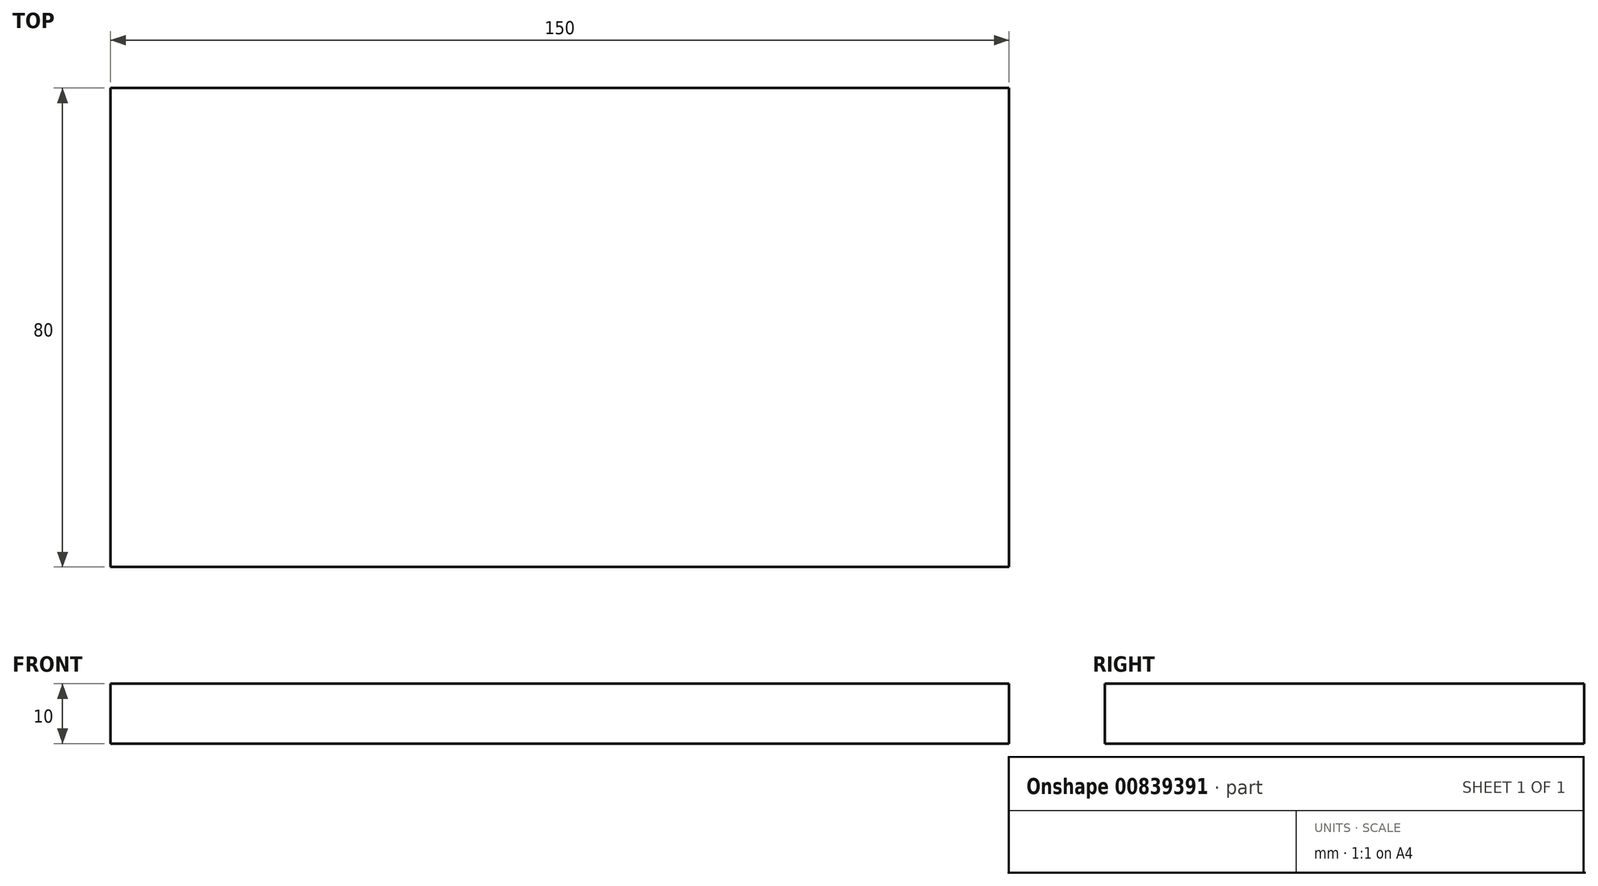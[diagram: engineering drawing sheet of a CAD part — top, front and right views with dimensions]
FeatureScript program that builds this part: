
annotation { "Feature Type Name" : "Feature", "Feature Type Description" : "" }
export const myFeature = defineFeature(function(context is Context, id is Id, definition is map)
    precondition{}
    {
        {
            var Q0;
            Q0=qCreatedBy(makeId("Top.planeOp"),FACE);
            var sketch = newSketch(context, id + "F0", { "sketchPlane" : qUnion([Q0])});
            skLineSegment(sketch, "E0.bottom", {"start": v(-48.92, 49.38) * mm, "end": v(51.08, 49.38) * mm});
            skLineSegment(sketch, "E0.top", {"start": v(-48.92, -50.62) * mm, "end": v(51.08, -50.62) * mm});
            skLineSegment(sketch, "E0.left", {"start": v(-48.92, 49.38) * mm, "end": v(-48.92, -50.62) * mm});
            skLineSegment(sketch, "E0.right", {"start": v(51.08, 49.38) * mm, "end": v(51.08, -50.62) * mm});
            skSolve(sketch);
        }
        {
            var Q0;
            Q0=makeQuery(id+"F0.imprint","IMPRINT",FACE,{"disambiguationData":[TD([[makeQuery(id+"F0.imprint","IMPRINT",EDGE,{"derivedFrom":sQuery(id+"F0.wireOp",EDGE,"E0.bottom")}),-1.0]])]});
            var sketch = newSketch(context, id + "F1", { "sketchPlane" : qUnion([Q0])});
            skLineSegment(sketch, "E1.bottom", {"start": v(-49.26, 49.15) * mm, "end": v(50.74, 49.15) * mm});
            skLineSegment(sketch, "E1.top", {"start": v(-49.26, -50.85) * mm, "end": v(50.74, -50.85) * mm});
            skLineSegment(sketch, "E1.left", {"start": v(-49.26, 49.15) * mm, "end": v(-49.26, -50.85) * mm});
            skLineSegment(sketch, "E1.right", {"start": v(50.74, 49.15) * mm, "end": v(50.74, -50.85) * mm});
            skSolve(sketch);
        }
        {
            var Q0;
            {var subQ0=sQuery(id+"F1.wireOp",EDGE,"E1.right");var subQ1=sQuery(id+"F1.wireOp",EDGE,"E1.bottom");var subQ2=makeQuery(id+"F1.imprint","INTERSECT",VERTEX,{"derivedFrom":[subQ1,subQ0]});Q0=makeQuery(id+"F1.imprint","IMPRINT",FACE,{"disambiguationData":[TD([[makeQuery(id+"F1.imprint","IMPRINT",EDGE,{"disambiguationData":[TD([[subQ2,1.0]])],"derivedFrom":subQ1}),-1.0]])]});}
            var sketch = newSketch(context, id + "F2", { "sketchPlane" : qUnion([Q0])});
            skLineSegment(sketch, "E2.bottom", {"start": v(-39.95, 37.83) * mm, "end": v(110.05, 37.83) * mm});
            skLineSegment(sketch, "E2.top", {"start": v(-39.95, -42.17) * mm, "end": v(110.05, -42.17) * mm});
            skLineSegment(sketch, "E2.left", {"start": v(-39.95, 37.83) * mm, "end": v(-39.95, -42.17) * mm});
            skLineSegment(sketch, "E2.right", {"start": v(110.05, 37.83) * mm, "end": v(110.05, -42.17) * mm});
            skSolve(sketch);
        }
        {
            var Q0;
            Q0 = qSketchRegion(id + "F2", true);
            extrude(context, id + "F3", {"entities" : qUnion([Q0]), "depth" : 10 * mm, "offsetDistance" : 25 * mm});
        }
    });
